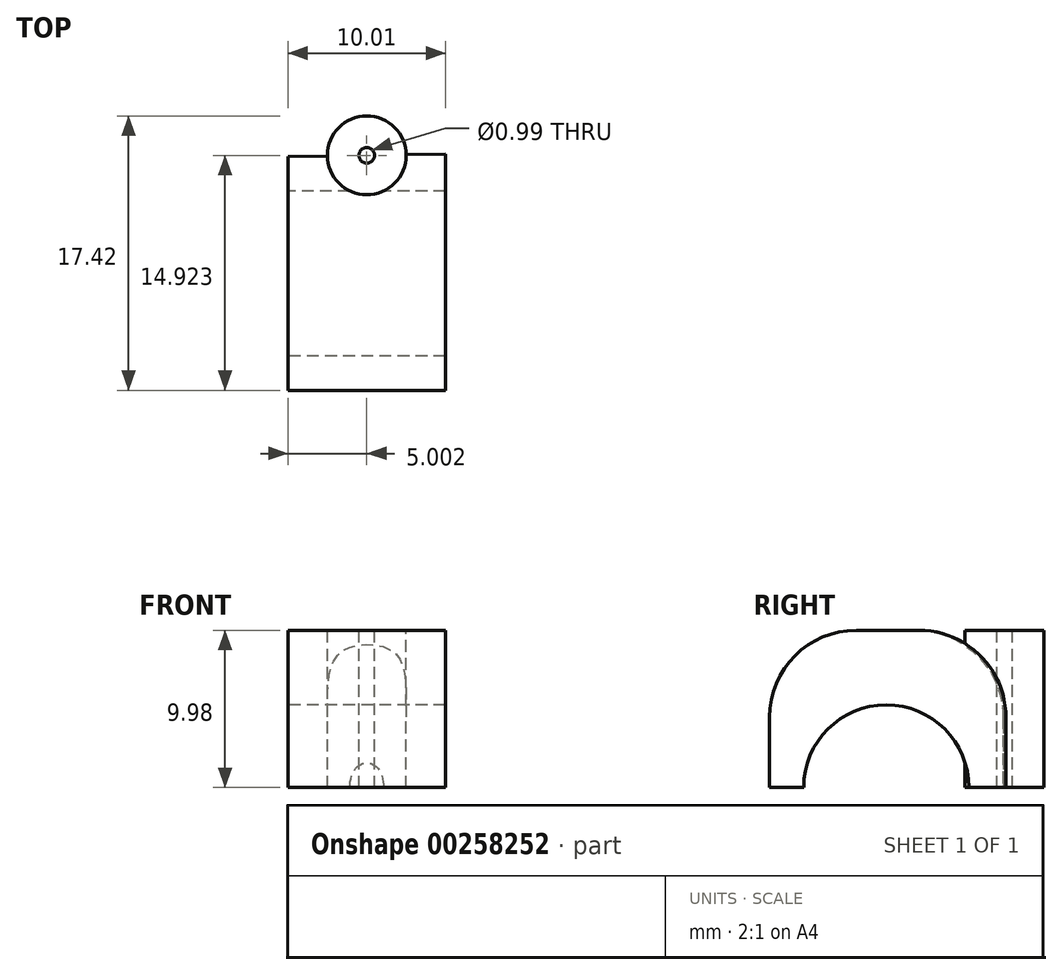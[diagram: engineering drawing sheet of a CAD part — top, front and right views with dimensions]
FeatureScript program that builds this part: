
annotation { "Feature Type Name" : "Feature", "Feature Type Description" : "" }
export const myFeature = defineFeature(function(context is Context, id is Id, definition is map)
    precondition{}
    {
        {
            var Q0;
            Q0=qCreatedBy(makeId("Top.planeOp"),FACE);
            var sketch = newSketch(context, id + "F0", { "sketchPlane" : qUnion([Q0])});
            skLineSegment(sketch, "E0", {"start": v(-14.14, -11.76) * mm, "end": v(-4.13, -11.76) * mm});
            skLineSegment(sketch, "E1", {"start": v(-4.13, -11.76) * mm, "end": v(-4.13, 3.25) * mm});
            skLineSegment(sketch, "E2", {"start": v(-14.14, -11.76) * mm, "end": v(-14.14, 3.07) * mm});
            skLineSegment(sketch, "E3", {"start": v(-14.14, 3.07) * mm, "end": v(-4.13, 3.25) * mm});
            skSolve(sketch);
        }
        {
            var Q0;
            Q0=makeQuery(id+"F0.imprint","IMPRINT",FACE,{"disambiguationData":[TD([[makeQuery(id+"F0.imprint","IMPRINT",EDGE,{"derivedFrom":sQuery(id+"F0.wireOp",EDGE,"E0")}),1.0]])]});
            extrude(context, id + "F1", {"entities" : qUnion([Q0]), "depth" : 7.5 * mm});
        }
        {
            var Q0;
            Q0=makeQuery(id+"F1.opExtrude","SWEPT_FACE",FACE,{"disambiguationData":[OSD([sQuery(id+"F0.wireOp",EDGE,"E2")])]});
            var sketch = newSketch(context, id + "F2", { "sketchPlane" : qUnion([Q0])});
            skArc(sketch, "E4", {"start": v(9.59, 0) * mm, "mid": v(4.34, 5.25) * mm, "end": v(-0.9, 0) * mm});
            skLineSegment(sketch, "E5.0", {"start": v(9.59, 0) * mm, "end": v(-0.9, 0) * mm});
            skPoint(sketch, "E6.orphan", {"position": v(11.76, 0) * mm});
            skPoint(sketch, "E7.orphan", {"position": v(-3.07, 0) * mm});
            skSolve(sketch);
        }
        {
            var Q0;
            Q0=makeQuery(id+"F2.imprint","IMPRINT",FACE,{"disambiguationData":[TD([[makeQuery(id+"F2.imprint","IMPRINT",EDGE,{"derivedFrom":sQuery(id+"F2.wireOp",EDGE,"E4")}),1.0]])]});
            extrude(context, id + "F3", {"entities" : qUnion([Q0]), "operationType" : NewBodyOperationType.REMOVE, "endBound" : BoundingType.THROUGH_ALL, "oppositeDirection" : true, "depth" : 25.4 * mm});
        }
        {
            var Q0;
            Q0=makeQuery(id+"F1.opExtrude","CAP_FACE",FACE,{"disambiguationData":[OSD([sQuery(id+"F0.wireOp",EDGE,"E0"),sQuery(id+"F0.wireOp",EDGE,"E1"),sQuery(id+"F0.wireOp",EDGE,"E2"),sQuery(id+"F0.wireOp",EDGE,"E3")])],"isStart":false});
            var sketch = newSketch(context, id + "F4", { "sketchPlane" : qUnion([Q0])});
            skLineSegment(sketch, "E8", {"start": v(-14.14, 3.07) * mm, "end": v(-4.13, 3.25) * mm});
            skLineSegment(sketch, "E9", {"start": v(-4.13, 3.25) * mm, "end": v(-4.13, -11.76) * mm});
            skLineSegment(sketch, "E10", {"start": v(-4.13, -11.76) * mm, "end": v(-14.14, -11.76) * mm});
            skLineSegment(sketch, "E11", {"start": v(-14.14, -11.76) * mm, "end": v(-14.14, 3.07) * mm});
            skSolve(sketch);
        }
        {
            var Q0;
            Q0 = qSketchRegion(id + "F4", true);
            extrude(context, id + "F5", {"entities" : qUnion([Q0]), "operationType" : NewBodyOperationType.ADD, "depth" : 2.5 * mm});
        }
        {
            var Q0;
            Q0=makeQuery(id+"F5.opExtrude","CAP_EDGE",EDGE,{"disambiguationData":[OSD([sQuery(id+"F4.wireOp",EDGE,"E8")])],"isStart":false});
            var Q1;
            Q1=makeQuery(id+"F5.opExtrude","CAP_EDGE",EDGE,{"disambiguationData":[OSD([sQuery(id+"F4.wireOp",EDGE,"E10")])],"isStart":false});
            fillet(context, id + "F6", {"entities" : qUnion([Q0, Q1]), "radius" : 5.5 * mm, "tangentPropagation" : true, "allowEdgeOverflow" : false});
        }
        {
            var Q0;
            Q0=makeQuery(id+"F5.opExtrude","CAP_FACE",FACE,{"disambiguationData":[OSD([sQuery(id+"F4.wireOp",EDGE,"E8"),sQuery(id+"F4.wireOp",EDGE,"E9"),sQuery(id+"F4.wireOp",EDGE,"E10"),sQuery(id+"F4.wireOp",EDGE,"E11")])],"isStart":false});
            var sketch = newSketch(context, id + "F7", { "sketchPlane" : qUnion([Q0])});
            skCircle(sketch, "E12", {"center": v(-9.14, 3.16) * mm, "radius": 2.5 * mm});
            skSolve(sketch);
        }
        {
            var Q0;
            Q0=makeQuery(id+"F7.imprint","IMPRINT",FACE,{"disambiguationData":[TD([[makeQuery(id+"F7.imprint","IMPRINT",EDGE,{"derivedFrom":sQuery(id+"F7.wireOp",EDGE,"E12")}),1.0]])]});
            extrude(context, id + "F8", {"entities" : qUnion([Q0]), "operationType" : NewBodyOperationType.ADD, "oppositeDirection" : true, "depth" : 9.98 * mm});
        }
        {
            var Q0;
            Q0=makeQuery(id+"F8.opExtrude","CAP_FACE",FACE,{"disambiguationData":[OSD([sQuery(id+"F7.wireOp",EDGE,"E12")])],"isStart":true});
            var sketch = newSketch(context, id + "F9", { "sketchPlane" : qUnion([Q0])});
            skCircle(sketch, "E13", {"center": v(-9.14, 3.16) * mm, "radius": 0.5 * mm});
            skSolve(sketch);
        }
        {
            var Q0;
            Q0 = qSketchRegion(id + "F9", true);
            extrude(context, id + "F10", {"entities" : qUnion([Q0]), "operationType" : NewBodyOperationType.REMOVE, "oppositeDirection" : true, "depth" : 9.98 * mm});
        }
    });
